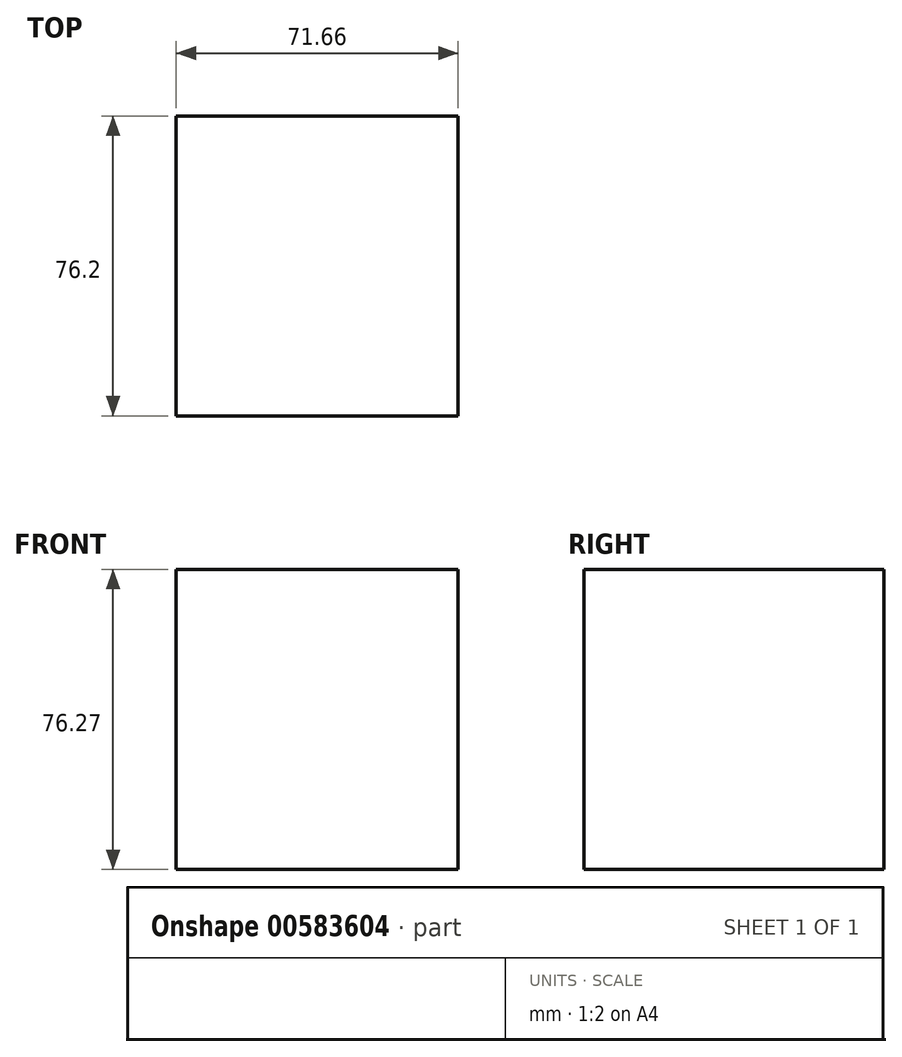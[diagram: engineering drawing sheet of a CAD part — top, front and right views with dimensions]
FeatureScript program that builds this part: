
annotation { "Feature Type Name" : "Feature", "Feature Type Description" : "" }
export const myFeature = defineFeature(function(context is Context, id is Id, definition is map)
    precondition{}
    {
        {
            var Q0;
            Q0=qCreatedBy(makeId("Front.planeOp"),FACE);
            var sketch = newSketch(context, id + "F0", { "sketchPlane" : qUnion([Q0])});
            skLineSegment(sketch, "E0.bottom", {"start": v(-36.98, 0.43) * mm, "end": v(34.68, 0.43) * mm});
            skLineSegment(sketch, "E0.top", {"start": v(-36.98, -75.84) * mm, "end": v(34.68, -75.84) * mm});
            skLineSegment(sketch, "E0.left", {"start": v(-36.98, 0.43) * mm, "end": v(-36.98, -75.84) * mm});
            skLineSegment(sketch, "E0.right", {"start": v(34.68, 0.43) * mm, "end": v(34.68, -75.84) * mm});
            skSolve(sketch);
        }
        {
            var Q0;
            Q0 = qSketchRegion(id + "F0", true);
            extrude(context, id + "F1", {"entities" : qUnion([Q0]), "oppositeDirection" : true, "depth" : 76.2 * mm, "offsetDistance" : 25.4 * mm});
        }
    });
